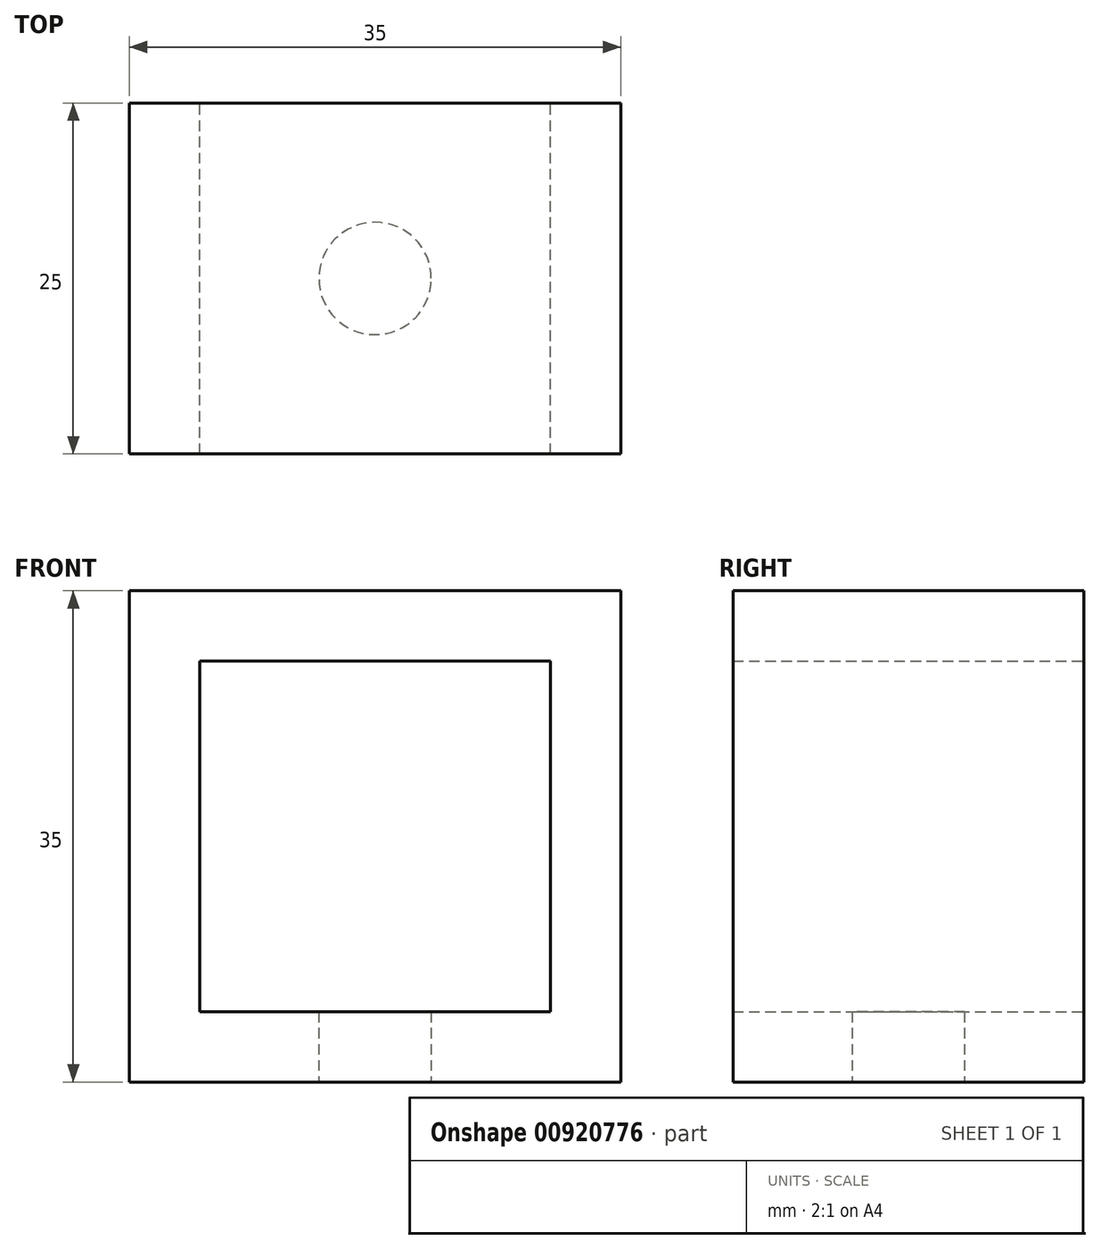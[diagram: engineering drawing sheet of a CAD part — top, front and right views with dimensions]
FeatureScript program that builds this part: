
annotation { "Feature Type Name" : "Feature", "Feature Type Description" : "" }
export const myFeature = defineFeature(function(context is Context, id is Id, definition is map)
    precondition{}
    {
        {
            var Q0;
            Q0=qCreatedBy(makeId("Front.planeOp"),FACE);
            var sketch = newSketch(context, id + "F0", { "sketchPlane" : qUnion([Q0])});
            skLineSegment(sketch, "E0.bottom", {"start": v(12.5, 12.5) * mm, "end": v(-12.5, 12.5) * mm});
            skLineSegment(sketch, "E0.top", {"start": v(12.5, -12.5) * mm, "end": v(-12.5, -12.5) * mm});
            skLineSegment(sketch, "E0.left", {"start": v(12.5, 12.5) * mm, "end": v(12.5, -12.5) * mm});
            skLineSegment(sketch, "E0.right", {"start": v(-12.5, 12.5) * mm, "end": v(-12.5, -12.5) * mm});
            skPoint(sketch, "E0.middle", {"position": v(0, 0) * mm});
            skLineSegment(sketch, "E1.bottom", {"start": v(17.5, 17.5) * mm, "end": v(-17.5, 17.5) * mm});
            skLineSegment(sketch, "E1.top", {"start": v(17.5, -17.5) * mm, "end": v(-17.5, -17.5) * mm});
            skLineSegment(sketch, "E1.left", {"start": v(17.5, 17.5) * mm, "end": v(17.5, -17.5) * mm});
            skLineSegment(sketch, "E1.right", {"start": v(-17.5, 17.5) * mm, "end": v(-17.5, -17.5) * mm});
            skSolve(sketch);
        }
        {
            var Q0;
            Q0 = qSketchRegion(id + "F0", true);
            extrude(context, id + "F1", {"entities" : qUnion([Q0]), "depth" : 25 * mm, "offsetDistance" : 25 * mm});
        }
        {
            var Q0;
            Q0=makeQuery(id+"F1.opExtrude","SWEPT_FACE",FACE,{"disambiguationData":[OSD([sQuery(id+"F0.wireOp",EDGE,"E1.top")])]});
            var sketch = newSketch(context, id + "F2", { "sketchPlane" : qUnion([Q0])});
            skLineSegment(sketch, "E2", {"start": v(-17.5, 25) * mm, "end": v(17.5, 0) * mm, "construction": true});
            skCircle(sketch, "E3", {"center": v(0, 12.5) * mm, "radius": 4 * mm});
            skSolve(sketch);
        }
        {
            var Q0;
            Q0 = qSketchRegion(id + "F2", true);
            extrude(context, id + "F3", {"entities" : qUnion([Q0]), "operationType" : NewBodyOperationType.REMOVE, "oppositeDirection" : true, "depth" : 25 * mm, "offsetDistance" : 25 * mm});
        }
    });
